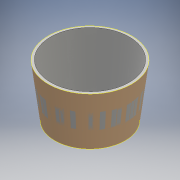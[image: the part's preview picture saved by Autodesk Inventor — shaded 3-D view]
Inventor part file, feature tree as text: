
AUTODESK INVENTOR PART (.ipt)
format: ipt  version: 2016 (Build 200138000, 138)  size: 116,736 bytes
history: native  units: mm
features: sketch x2, plane x1, thicken_offset x1, other x1, loft x1
ambient origin geometry x8: Origin, YZ Plane, XZ Plane, XY Plane, X Axis, Y Axis, Z Axis, Center Point
bodies: Body1 (feature_tree), Body2 (feature_tree)
feature tree (6):
  sketch  "Sketch1"  dims[d0=324.0mm d1=9.52mm]
  plane  "Work Plane1"
  thicken_offset  "Thicken1"
  sketch  "Sketch2"  dims[d2=-203.0mm d3=273.0mm d4=9.52mm d15=0.0mm d16=90.0deg d17=0.0mm d18=90.0deg d19=9.52mm d20=9.52mm]
  other  "Srf1"
  loft  "LoftSrf1"
